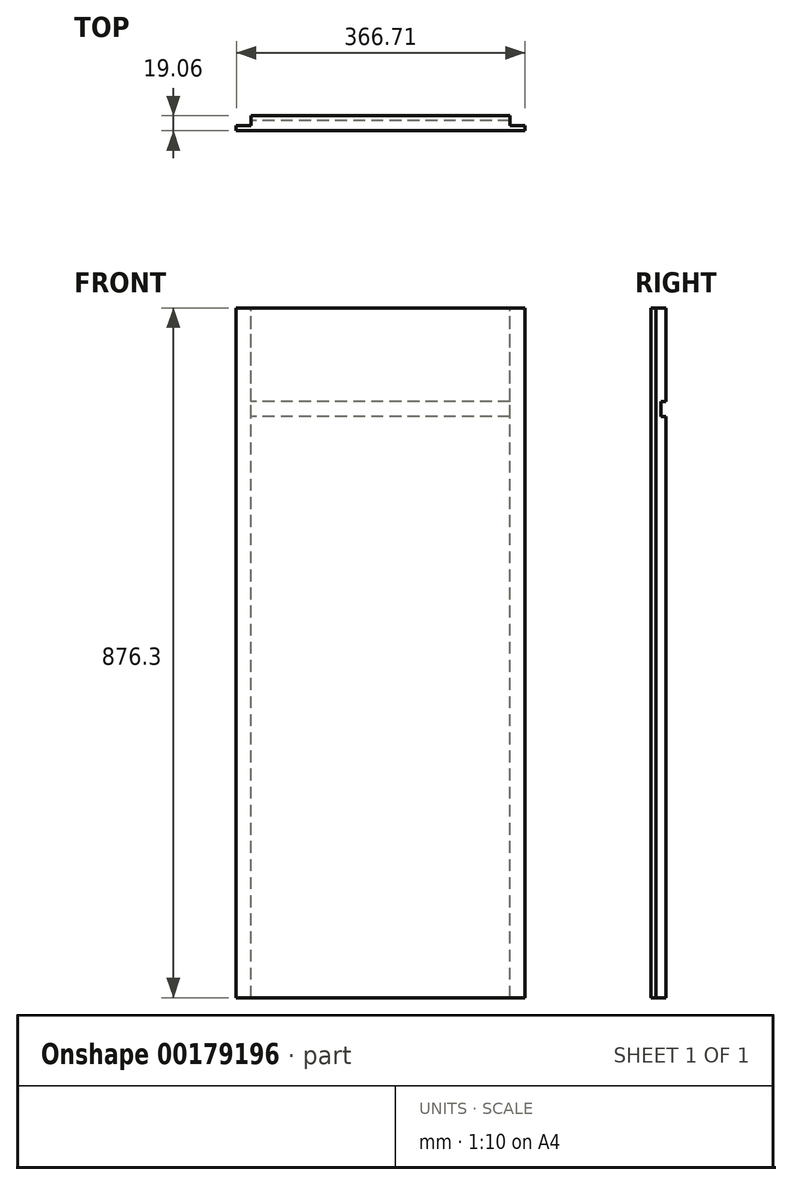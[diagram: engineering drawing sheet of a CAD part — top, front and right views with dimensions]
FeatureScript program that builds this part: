
annotation { "Feature Type Name" : "Feature", "Feature Type Description" : "" }
export const myFeature = defineFeature(function(context is Context, id is Id, definition is map)
    precondition{}
    {
        {
            var Q0;
            Q0=qCreatedBy(makeId("Front.planeOp"),FACE);
            var sketch = newSketch(context, id + "F0", { "sketchPlane" : qUnion([Q0])});
            skLineSegment(sketch, "E0.bottom", {"start": v(-247.9, 438.15) * mm, "end": v(118.8, 438.15) * mm});
            skLineSegment(sketch, "E0.top", {"start": v(-247.9, -438.15) * mm, "end": v(118.8, -438.15) * mm});
            skLineSegment(sketch, "E0.left", {"start": v(-247.9, 438.15) * mm, "end": v(-247.9, -438.15) * mm});
            skLineSegment(sketch, "E0.right", {"start": v(118.8, 438.15) * mm, "end": v(118.8, -438.15) * mm});
            skLineSegment(sketch, "E1", {"start": v(-247.9, 0) * mm, "end": v(118.8, 0) * mm});
            skSolve(sketch);
        }
        {
            var Q0;
            {var subQ0=sQuery(id+"F0.wireOp",EDGE,"E0.bottom");Q0=makeQuery(id+"F0.imprint","IMPRINT",FACE,{"disambiguationData":[TD([[makeQuery(id+"F0.imprint","IMPRINT",EDGE,{"derivedFrom":subQ0}),-1.0]])]});}
            var Q1;
            {var subQ0=sQuery(id+"F0.wireOp",EDGE,"E0.top");Q1=makeQuery(id+"F0.imprint","IMPRINT",FACE,{"disambiguationData":[TD([[makeQuery(id+"F0.imprint","IMPRINT",EDGE,{"derivedFrom":subQ0}),1.0]])]});}
            extrude(context, id + "F1", {"entities" : qUnion([Q0, Q1]), "depth" : 19.05 * mm, "symmetric" : true});
        }
        {
            var Q0;
            Q0=makeQuery(id+"F1.opExtrude","CAP_FACE",FACE,{"disambiguationData":[OSD([sQuery(id+"F0.wireOp",EDGE,"E0.bottom"),sQuery(id+"F0.wireOp",EDGE,"E0.top"),sQuery(id+"F0.wireOp",EDGE,"E0.left"),sQuery(id+"F0.wireOp",EDGE,"E0.right")])],"isStart":true});
            var sketch = newSketch(context, id + "F2", { "sketchPlane" : qUnion([Q0])});
            skLineSegment(sketch, "E2.bottom", {"start": v(-118.8, 300.04) * mm, "end": v(247.9, 300.04) * mm});
            skLineSegment(sketch, "E2.top", {"start": v(-118.8, 319.09) * mm, "end": v(247.9, 319.09) * mm});
            skLineSegment(sketch, "E2.left", {"start": v(-118.8, 300.04) * mm, "end": v(-118.8, 319.09) * mm});
            skLineSegment(sketch, "E2.right", {"start": v(247.9, 300.04) * mm, "end": v(247.9, 319.09) * mm});
            skSolve(sketch);
        }
        {
            var Q0;
            Q0=makeQuery(id+"F2.imprint","IMPRINT",FACE,{"disambiguationData":[TD([[makeQuery(id+"F2.imprint","IMPRINT",EDGE,{"derivedFrom":sQuery(id+"F2.wireOp",EDGE,"E2.bottom")}),1.0]])]});
            extrude(context, id + "F3", {"entities" : qUnion([Q0]), "operationType" : NewBodyOperationType.REMOVE, "oppositeDirection" : true, "depth" : 6.35 * mm});
        }
        {
            var Q0;
            {var subQ0=sQuery(id+"F0.wireOp",EDGE,"E0.top");var subQ1=sQuery(id+"F0.wireOp",EDGE,"E0.left");var subQ2=sQuery(id+"F0.wireOp",EDGE,"E0.right");Q0=makeQuery(id+"F3.boolean.opBoolean","SPLIT",FACE,{"disambiguationData":[TD([makeQuery(id+"F1.opExtrude","SWEPT_FACE",FACE,{"disambiguationData":[OSD([subQ0])]})])],"derivedFrom":makeQuery(id+"F1.opExtrude","CAP_FACE",FACE,{"disambiguationData":[OSD([sQuery(id+"F0.wireOp",EDGE,"E0.bottom"),subQ0,subQ1,subQ2])],"isStart":true})});}
            var sketch = newSketch(context, id + "F4", { "sketchPlane" : qUnion([Q0])});
            skLineSegment(sketch, "E3.bottom", {"start": v(-118.8, -438.15) * mm, "end": v(-99.76, -438.15) * mm});
            skLineSegment(sketch, "E3.top", {"start": v(-118.8, 438.15) * mm, "end": v(-99.76, 438.15) * mm});
            skLineSegment(sketch, "E3.left", {"start": v(-118.8, -438.15) * mm, "end": v(-118.8, 438.15) * mm});
            skLineSegment(sketch, "E3.right", {"start": v(-99.76, -438.15) * mm, "end": v(-99.76, 438.15) * mm});
            skLineSegment(sketch, "E4.bottom", {"start": v(247.9, -438.15) * mm, "end": v(228.85, -438.15) * mm});
            skLineSegment(sketch, "E4.top", {"start": v(247.9, 438.15) * mm, "end": v(228.85, 438.15) * mm});
            skLineSegment(sketch, "E4.left", {"start": v(247.9, -438.15) * mm, "end": v(247.9, 438.15) * mm});
            skLineSegment(sketch, "E4.right", {"start": v(228.85, -438.15) * mm, "end": v(228.85, 438.15) * mm});
            skSolve(sketch);
        }
        {
            var Q0;
            {var subQ0=sQuery(id+"F4.wireOp",EDGE,"E3.bottom");Q0=makeQuery(id+"F4.imprint","IMPRINT",FACE,{"disambiguationData":[TD([[makeQuery(id+"F4.imprint","IMPRINT",EDGE,{"derivedFrom":subQ0}),-1.0]])]});}
            var Q1;
            {var subQ0=sQuery(id+"F4.wireOp",EDGE,"E3.top");Q1=makeQuery(id+"F4.imprint","IMPRINT",FACE,{"disambiguationData":[TD([[makeQuery(id+"F4.imprint","IMPRINT",EDGE,{"derivedFrom":subQ0}),-1.0]])]});}
            var Q2;
            {var subQ0=sQuery(id+"F4.wireOp",EDGE,"E4.top");Q2=makeQuery(id+"F4.imprint","IMPRINT",FACE,{"disambiguationData":[TD([[makeQuery(id+"F4.imprint","IMPRINT",EDGE,{"derivedFrom":subQ0}),1.0]])]});}
            var Q3;
            {var subQ0=sQuery(id+"F4.wireOp",EDGE,"E4.bottom");Q3=makeQuery(id+"F4.imprint","IMPRINT",FACE,{"disambiguationData":[TD([[makeQuery(id+"F4.imprint","IMPRINT",EDGE,{"derivedFrom":subQ0}),-1.0]])]});}
            extrude(context, id + "F5", {"entities" : qUnion([Q0, Q1, Q2, Q3]), "operationType" : NewBodyOperationType.REMOVE, "oppositeDirection" : true, "depth" : 12.7 * mm});
        }
    });
